# Revit family: Revolving-Door-Stanley-500_Series
name_source: partatom
category: Doors
revit_build: Autodesk Revit 2013 (Build: 20130531_2115(x64)
units: mm (PartAtom-declared; Revit-internal decimal feet)

## types (1)
- 4 Panel
    Appear In Schedule = No
    Assembly Code = C1020210
    CTRL Frame Opening Width = 55.25 "
    Description = Relvolving Aluminum
    Frame Opening Width = 53.25 "
    Frame Width = 1.5 "
    Glazing Thickness Panel = 0.25 "
    Hardware Finish = Metal - Stanley - Aluminum - Anodized - Clear CL2
    Manufacturer = Stanley Access Technologies
    Model = Series 500 Revilving Door
    Opening Thickness Offset = 0.125 "
    Panel Bottom Rail Height = 4 "
    Panel Finish = Metal - Stanley - Aluminum - Anodized - Clear CL2
    Product Page URL = http://www.stanleyaccesstechnologies.com
    Type Comments = Manual
    URL = http://www.stanleyaccess.com
    Wall Closure = By host

## geometry (parser evidence)
native form markers: Blend x24, Sweep x7
no freeform markers — native parametric forms only
